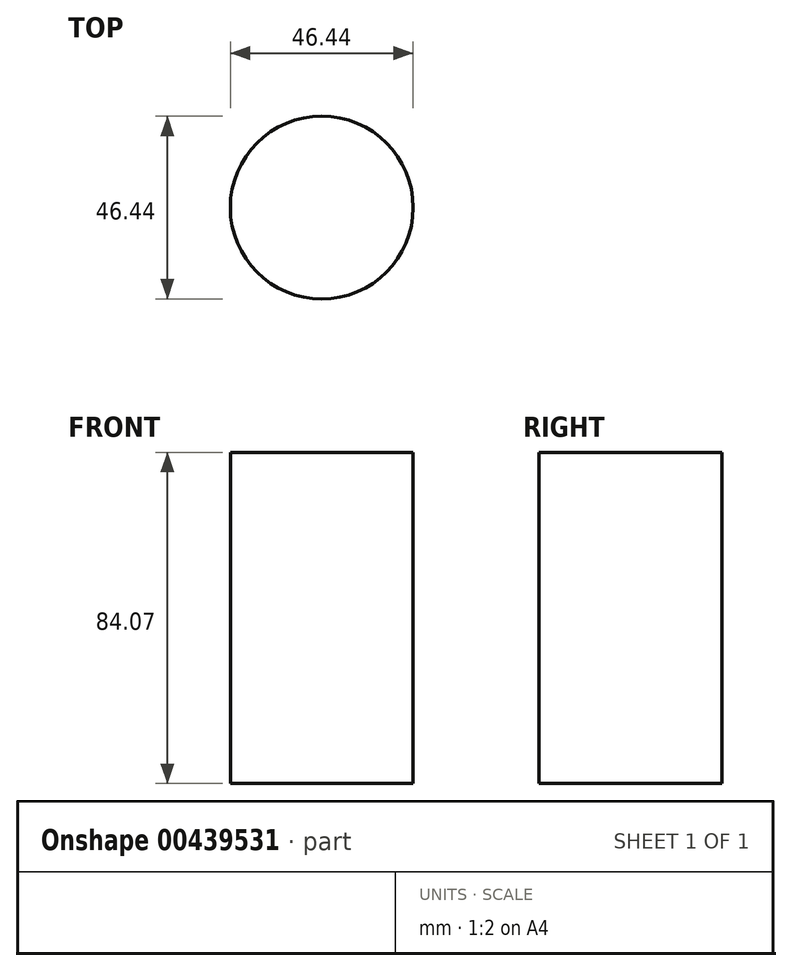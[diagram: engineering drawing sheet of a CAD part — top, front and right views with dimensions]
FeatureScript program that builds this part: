
annotation { "Feature Type Name" : "Feature", "Feature Type Description" : "" }
export const myFeature = defineFeature(function(context is Context, id is Id, definition is map)
    precondition{}
    {
        {
            var Q0;
            Q0=qCreatedBy(makeId("Top.planeOp"),FACE);
            var sketch = newSketch(context, id + "F0", { "sketchPlane" : qUnion([Q0])});
            skCircle(sketch, "E0", {"center": v(0, 0) * mm, "radius": 23.22 * mm});
            skSolve(sketch);
        }
        {
            var Q0;
            Q0=makeQuery(id+"F0.imprint","IMPRINT",FACE,{"disambiguationData":[TD([[makeQuery(id+"F0.imprint","IMPRINT",EDGE,{"derivedFrom":sQuery(id+"F0.wireOp",EDGE,"E0")}),1.0]])]});
            extrude(context, id + "F1", {"entities" : qUnion([Q0]), "depth" : 84.07 * mm});
        }
    });
